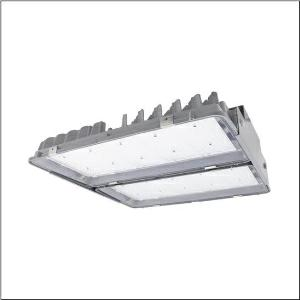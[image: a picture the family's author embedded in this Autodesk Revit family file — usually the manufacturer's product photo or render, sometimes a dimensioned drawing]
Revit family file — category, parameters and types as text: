
# Revit family: highbay_11xtreme_51hf82db4wma
name_source: partatom
category: Lighting Fixtures
units: mm (PartAtom-declared; Revit-internal decimal feet)

## family parameters
Cut with Voids When Loaded = No
Host = Face
Light Source = No
Part Type = Normal
Room Calculation Point = No
Round Connector Dimension = Use Diameter
Shared = No

## types (1)
- --- (1 x LED, 75000 lm, 422.2 W, 4000K)
    Apparent Load = 422 VA
    CIE Flux Codes = 84 96 100 100 100
    Color Rendering = 80
    Color Temperature = 4000K
    Default Elevation = 1800 mm
    Description = Highbay 11Xtreme, LED high bay luminaire, primary light control with lens, of PMMA, primary optical cover: cover, of toughened safety glass, light emission: direct distribution, primary light characteristic: symmetric, installation type: suspended mounting, surface-mounted, 2x LED module,for 1x 2x LED, rated luminous flux: 75.000lm, luminous efficacy: 178lm/W, light colour: 840, colour temperature: 4000K, with cable H07RN-F 5x 1.5mm², mains connection: 220..240V, AC, 50/60Hz, cable length: 1,5m, rated input power: 422W, luminaire housing, of diecast aluminium, partly coated, silver, length: 595mm, width: 560mm, height: 195mm, protection rating (complete): IP66, insulation class (complete): insulation class I (protective earthing), certification: CE, ENEC, UKCA, protection symbol: D, ball protection: ball impact resistant according to DIN VDE 0710 part 13 (with chain suspension), impact resistance: IK08, permissible operating ambient temperature: -25..+45°C, reducing of maximum allowable ambient temperature of 5°C with ceiling mounting, packaging unit: 1 piece
    Height = 157 mm
    Lamp = 1 x LED
    Lamp Light Flux = 75000 lm
    Lamp Power = 422.2 W
    Lamp count = 1
    Length = 593 mm
    Luminous efficacy = 178 lm/W
    Manufacturer = Siteco
    ModVariant = No
    Model = 51HF82DB4WMA
    Mounting Place = Ceiling
    Mounting Type = Pendant
    Number of Poles = 1
    OnlyDefault = Yes
    Power Factor = 1
    Product Name = Highbay 11Xtreme
    Product group = LED high bay luminaire
    ProductGroupID = 903
    Protection Class = Protection class I
    Protection Degree = IP 66
    RLX_Detail_Level = 1
    RLX_Emergency_Light_Flux = 0 lm
    RLX_Emergency_Type = 0
    RLX_Emergency_Type_DB = No
    RlxData = <blob elided: 34349 chars, md5=64485901>
    Socket = socket
    Standby Power = 0 W
    System Light Flux = 75000 lm
    System Power = 422 W
    Type Comments = factory setting: luminous flux: 100 % | dim-lin: 254 | 1389 mA
    Type Image = l_1258340.jpg
    URL = http://relux.com
    VarID = @adj_035587
    Voltage = 0 V
    Weight = 0.00 kg
    Width = 568 mm

## geometry (parser evidence)
native form markers: Blend x4, Sweep x10
no freeform markers — native parametric forms only
